# Revit family: PRD_AR_WshbsnTps_F5EElectronicWashbasinTap_F5EV1017
name_source: partatom
category: Plumbing Fixtures
units: mm (PartAtom-declared; Revit-internal decimal feet)

## family parameters
Cut with Voids When Loaded = Yes
Enable Cutting in Views = Yes
Host = Face
Maintain Annotation Orientation = No
OmniClass Number = 23.45.05.14.99
OmniClass Title = Other Sanitary Washing Plumbing Fixtures
Part Type = Normal
Room Calculation Point = No
Round Connector Dimension = Use Diameter
Shared = No

## types (1)
- F5EV1017
    AdjustableFlowTime = Yes
    AssetType = Fixed
    BIMObjectName = PRD_AR_WashbasinTaps_F5EElectronicWashbasinTap_F5EV1017
    BodyMaterial = PRD_AR_StainlessSteel_Brushed
    BuiltInFittingModel = Finishing section
    ButtonMaterial = PRD_AR_ChromatedBrass_HighPolished
    CW Connection = Yes
    CWFU = 0
    Category = Pr_40_20_87_98, Washbasin taps
    CloseOffRating = 0.0 Pa
    CompatibleA3000Open = Yes
    CoverPlateHeight = 245
    CoverPlateWidth = 190
    Default Elevation = 1219 mm
    DefaultAutomaticHygieneFlush = 24h after the last activity
    DefaultFlowTime = 10 Seconds
    Depressurised = No
    Description = F5E - A3000 open washbasin tap DN 15 as finished installation kit for in-wall installation in the basic installation kit, for sanitary facilities. Especially suitable for facilities at risk of vandalism. Electronically controlled, for connection to pre-mixed hot water or cold water. With waterproof electronic module and electric T-junction for connection to system cable, solenoid valve, stainless steel cover plate 190 x 245 x 2 mm, mounting from the front with safety screws, including piezo push-button with start/stop function and recess for KWC wall outlet DN 15 (required separately). Depth adjustability 20 mm. Activated hygiene flushing 24 hours after the last activity. With facility for parameterization, cleaning deactivation and communication via ECC2 function controller, 24 V DC.
    DiameterNominal = DN 15
    Export Type to IFC As = IfcSanitaryTerminalType
    FaucetFunction = UNSET
    FaucetOperation = SELFCLOSING
    FaucetType = UNSET
    Features = For connection to pre-mixed hot water or cold water. Stainless steel cover plate 190 x 245 x 2 mm, mounting from the front with safety screws. Wall outlet must be ordered separately.
    Finish = Stainless steel satin finished
    Flow = 0.5 L/s
    FlowCoefficient = 0.46 l/s
    FunctionalPrinciple = electronic self-closing
    HW Connection = Yes
    HWFU = 0
    HygieneFlushing = Yes
    IfcExportAs = IfcValveType
    IfcExportType = FAUCET
    LockingMechanism = Top section, non-ceramic
    Manufacturer = KWC Group Management AG
    ManufacturerName = KWC Group Management AG
    ManufacturerURL = www.kwc-professional.com
    Material = stainless steel
    MaterialCodeCasing = 1.4301 Chrome Nickel steel V2A
    MaterialFitting = brass-look
    MaximumFlowTime = 6500 Seconds
    MinimumFlowPressure = 1 bar
    MinimumFlowTime = 1 Seconds
    Model = F5EV1017
    ModelNumber = 2030067880
    ModelReference = F5EV1017
    NBSDescription = Water supply fittings for wash basins and troughs
    NBSReference = 45-35-70/371
    Name = F5E Electronic washbasin tap F5EV1017
    NominalDepth = 2 mm  [stored 0.00656168 ft]
    NominalHeight = 245 mm  [stored 0.803806 ft]
    NominalWidth = 190 mm
    Parameterization = network
    PositionOfPowerConnection = from top
    PowerSupplyConnection = A3000 open 24 V DC
    ProductInformation = http://pim.kwc.com
    ProtectiveShutdown = Yes
    ProtectiveSystemIP = IP59K
    Size = 15
    SoundInsulation = No
    Status = New
    SurfaceFinishCasing = satin finished
    SurfaceFinishFitting = chromed
    TestPressure = 0.0 Pa
    Type IFC Predefined Type = USERDEFINED
    TypeOfMixing = No
    TypeOfMounting = in-wall installation with box
    TypeOfOperation = Sensor Operation
    TypeOfPowerSupply = Transformer
    TypeOfSensor = piezo-electronic sensor
    TypeOfTap = in-wall tap
    URL = www.kwc-professional.com
    Uniclass2015Code = Pr_40_20_87_98
    Uniclass2015Title = Washbasin taps
    Uniclass2015Version = Products v1.36
    ValveMechanism = OTHER
    ValveOperation = SOLENOID
    ValvePattern = STRAIGHT_2_PORT
    Vent Connection = Yes
    Version = 1
    VolumeFlowRateAt3Bar = 0.46 l/s
    WFU = 0
    Waste Connection = Yes
    WithFilter = Yes
    WithTransformerPowerSupply = No
    WorkingPressure = 0.0 Pa

note: [stored X ft] marks values corroborated as IEEE doubles in the binary element streams (Revit-internal decimal feet)

## geometry (parser evidence)
native form markers: Sweep x7
no freeform markers — native parametric forms only
